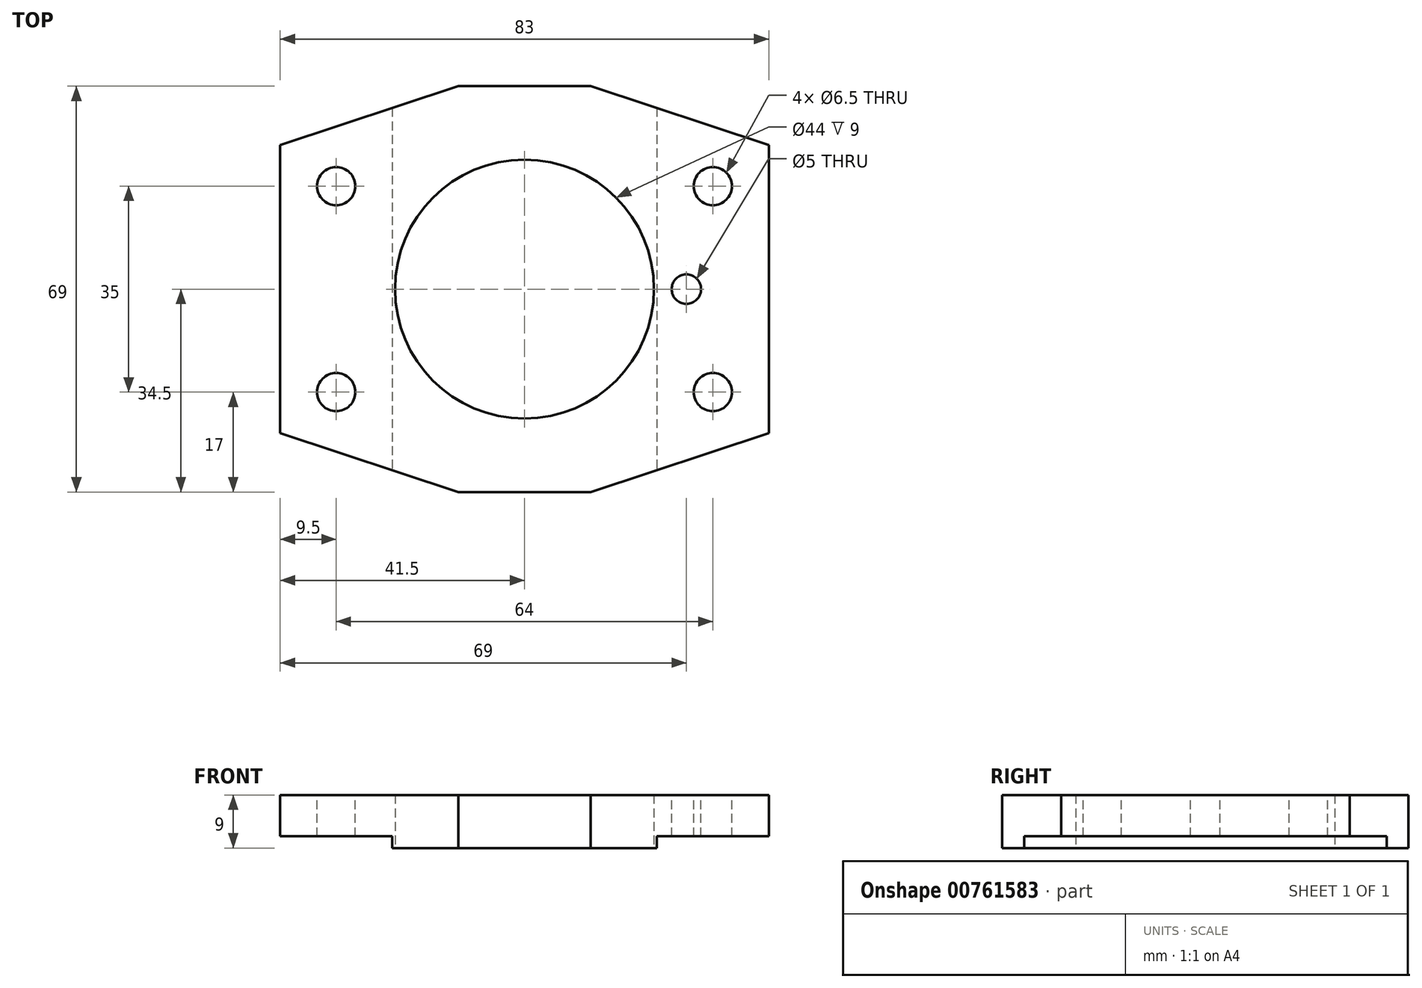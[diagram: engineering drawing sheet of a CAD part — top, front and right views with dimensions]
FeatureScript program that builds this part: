
annotation { "Feature Type Name" : "Feature", "Feature Type Description" : "" }
export const myFeature = defineFeature(function(context is Context, id is Id, definition is map)
    precondition{}
    {
        {
            var Q0;
            Q0=qCreatedBy(makeId("Top.planeOp"),FACE);
            var sketch = newSketch(context, id + "F0", { "sketchPlane" : qUnion([Q0])});
            skLineSegment(sketch, "E0", {"start": v(0, 22) * mm, "end": v(0, 34.5) * mm});
            skLineSegment(sketch, "E1", {"start": v(0, 34.5) * mm, "end": v(11.26, 34.5) * mm});
            skLineSegment(sketch, "E2", {"start": v(11.26, 34.5) * mm, "end": v(41.5, 24.5) * mm});
            skLineSegment(sketch, "E3", {"start": v(41.5, 24.5) * mm, "end": v(41.5, 0) * mm});
            skLineSegment(sketch, "E4", {"start": v(41.5, 0) * mm, "end": v(22, 0) * mm});
            skArc(sketch, "E5", {"start": v(22, 0) * mm, "mid": v(15.56, 15.56) * mm, "end": v(0, 22) * mm});
            skSolve(sketch);
        }
        {
            var Q0;
            Q0=makeQuery(id+"F0.imprint","IMPRINT",FACE,{"disambiguationData":[TD([[makeQuery(id+"F0.imprint","IMPRINT",EDGE,{"derivedFrom":sQuery(id+"F0.wireOp",EDGE,"E0")}),-1.0]])]});
            extrude(context, id + "F1", {"entities" : qUnion([Q0]), "depth" : 9 * mm, "offsetDistance" : 25 * mm});
        }
        {
            var Q0;
            Q0=qCreatedBy(makeId("Front.planeOp"),FACE);
            var sketch = newSketch(context, id + "F2", { "sketchPlane" : qUnion([Q0])});
            skLineSegment(sketch, "E6.bottom", {"start": v(22.5, 0) * mm, "end": v(41.5, 0) * mm});
            skLineSegment(sketch, "E6.top", {"start": v(22.5, 2) * mm, "end": v(41.5, 2) * mm});
            skLineSegment(sketch, "E6.left", {"start": v(22.5, 0) * mm, "end": v(22.5, 2) * mm});
            skLineSegment(sketch, "E6.right", {"start": v(41.5, 0) * mm, "end": v(41.5, 2) * mm});
            skSolve(sketch);
        }
        {
            var Q0;
            Q0 = qSketchRegion(id + "F2", true);
            extrude(context, id + "F3", {"entities" : qUnion([Q0]), "operationType" : NewBodyOperationType.REMOVE, "endBound" : BoundingType.THROUGH_ALL, "oppositeDirection" : true, "depth" : 25 * mm, "offsetDistance" : 25 * mm});
        }
        {
            var Q0;
            Q0=makeQuery(id+"F1.opExtrude","CAP_FACE",FACE,{"disambiguationData":[OSD([sQuery(id+"F0.wireOp",EDGE,"E0"),sQuery(id+"F0.wireOp",EDGE,"E1"),sQuery(id+"F0.wireOp",EDGE,"E2"),sQuery(id+"F0.wireOp",EDGE,"E3"),sQuery(id+"F0.wireOp",EDGE,"E4")])],"isStart":false});
            var sketch = newSketch(context, id + "F4", { "sketchPlane" : qUnion([Q0])});
            skPoint(sketch, "E7", {"position": v(27.5, 0) * mm});
            skPoint(sketch, "E8", {"position": v(32, 17.5) * mm});
            skSolve(sketch);
        }
        {
            var Q0;
            Q0=sQuery(id+"F4.wireOp",VERTEX,"E8");
            var Q1;
            Q1=makeQuery(id+"F1.opExtrude","SWEPT_BODY",BODY,{"disambiguationData":[OSD([sQuery(id+"F0.wireOp",EDGE,"E0"),sQuery(id+"F0.wireOp",EDGE,"E1"),sQuery(id+"F0.wireOp",EDGE,"E2"),sQuery(id+"F0.wireOp",EDGE,"E3"),sQuery(id+"F0.wireOp",EDGE,"E4")])]});
            hole(context, id + "F5", {"style" : HoleStyle.SIMPLE, "endStyle" : HoleEndStyle.THROUGH, "holeDiameter" : 6.5 * mm, "majorDiameter" : 8 * mm, "isTappedThrough" : true, "tappedDepth" : 7 * mm, "tapClearance" : 0, "startFromSketch" : true, "locations" : qUnion([Q0]), "scope" : qUnion([Q1])});
        }
        {
            var Q0;
            Q0=makeQuery(id+"F1.opExtrude","SWEPT_BODY",BODY,{"disambiguationData":[OSD([sQuery(id+"F0.wireOp",EDGE,"E0"),sQuery(id+"F0.wireOp",EDGE,"E1"),sQuery(id+"F0.wireOp",EDGE,"E2"),sQuery(id+"F0.wireOp",EDGE,"E3"),sQuery(id+"F0.wireOp",EDGE,"E4")])]});
            var Q1;
            Q1=qCreatedBy(makeId("Right.planeOp"),FACE);
            mirror(context, id + "F6", {"operationType" : NewBodyOperationType.ADD, "entities" : qUnion([Q0]), "mirrorPlane" : qUnion([Q1])});
        }
        {
            var Q0;
            Q0=makeQuery(id+"F1.opExtrude","SWEPT_BODY",BODY,{"disambiguationData":[OSD([sQuery(id+"F0.wireOp",EDGE,"E0"),sQuery(id+"F0.wireOp",EDGE,"E1"),sQuery(id+"F0.wireOp",EDGE,"E2"),sQuery(id+"F0.wireOp",EDGE,"E3"),sQuery(id+"F0.wireOp",EDGE,"E4")])]});
            var Q1;
            Q1=qCreatedBy(makeId("Front.planeOp"),FACE);
            mirror(context, id + "F7", {"operationType" : NewBodyOperationType.ADD, "entities" : qUnion([Q0]), "mirrorPlane" : qUnion([Q1])});
        }
        {
            var Q0;
            Q0=sQuery(id+"F4.wireOp",VERTEX,"E7");
            var Q1;
            Q1=makeQuery(id+"F1.opExtrude","SWEPT_BODY",BODY,{"disambiguationData":[OSD([sQuery(id+"F0.wireOp",EDGE,"E0"),sQuery(id+"F0.wireOp",EDGE,"E1"),sQuery(id+"F0.wireOp",EDGE,"E2"),sQuery(id+"F0.wireOp",EDGE,"E3"),sQuery(id+"F0.wireOp",EDGE,"E4")])]});
            hole(context, id + "F8", {"style" : HoleStyle.SIMPLE, "endStyle" : HoleEndStyle.THROUGH, "standardTappedOrClearance" : lookupTablePath({ "standard" : "ISO", "engagement" : "75%", "pitch" : "1 mm", "size" : "M6", "type" : "Tapped" }), "standardBlindInLast" : lookupTablePath({ "standard" : "ISO", "engagement" : "75%", "pitch" : "1 mm", "size" : "M6", "type" : "Tapped" }), "holeDiameter" : 5 * mm, "majorDiameter" : 6 * mm, "showTappedDepth" : true, "isTappedThrough" : true, "tappedDepth" : 7 * mm, "tapClearance" : 0, "startFromSketch" : true, "locations" : qUnion([Q0]), "scope" : qUnion([Q1])});
        }
    });
